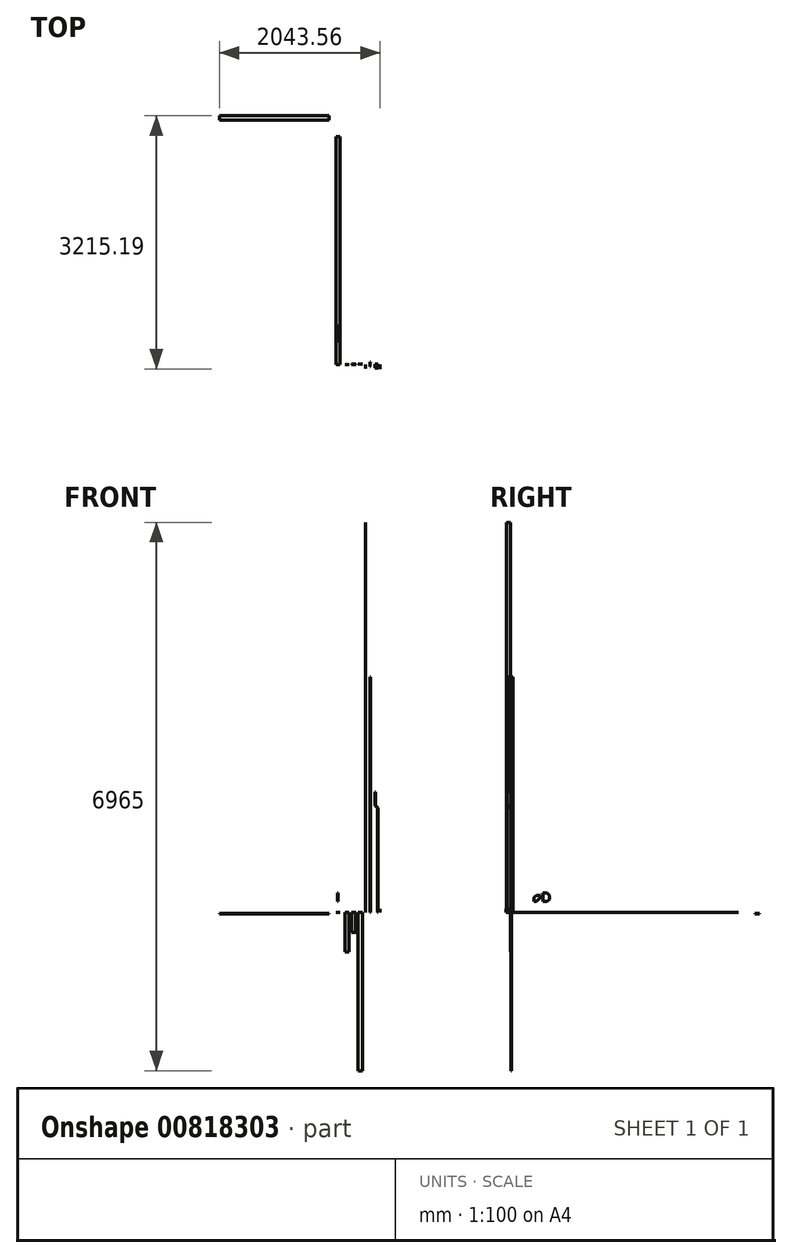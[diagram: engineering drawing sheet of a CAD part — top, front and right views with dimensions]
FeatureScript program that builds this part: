
annotation { "Feature Type Name" : "Feature", "Feature Type Description" : "" }
export const myFeature = defineFeature(function(context is Context, id is Id, definition is map)
    precondition{}
    {
        {
            var Q0;
            Q0=qCreatedBy(makeId("Front.planeOp"),FACE);
            var sketch = newSketch(context, id + "F0", { "sketchPlane" : qUnion([Q0])});
            skLineSegment(sketch, "E0.bottom", {"start": v(-26.5, 2.5) * mm, "end": v(26.5, 2.5) * mm});
            skLineSegment(sketch, "E0.left", {"start": v(-26.5, 2.5) * mm, "end": v(-26.5, -2.5) * mm});
            skLineSegment(sketch, "E0.right", {"start": v(26.5, 2.5) * mm, "end": v(26.5, -2.5) * mm});
            skPoint(sketch, "E0.middle", {"position": v(0, 0) * mm});
            skLineSegment(sketch, "E1", {"start": v(-26.5, -2.5) * mm, "end": v(-25, -2.5) * mm});
            skLineSegment(sketch, "E2", {"start": v(-25, -2.5) * mm, "end": v(-25, 1) * mm});
            skLineSegment(sketch, "E3", {"start": v(-25, 1) * mm, "end": v(25, 1) * mm});
            skLineSegment(sketch, "E4", {"start": v(25, 1) * mm, "end": v(25, -2.5) * mm});
            skLineSegment(sketch, "E5", {"start": v(25, -2.5) * mm, "end": v(26.5, -2.5) * mm});
            skSolve(sketch);
        }
        {
            var Q0;
            Q0 = qSketchRegion(id + "F0", true);
            extrude(context, id + "F1", {"entities" : qUnion([Q0]), "oppositeDirection" : true, "depth" : 2900 * mm, "offsetDistance" : 25 * mm});
        }
        {
            var Q0;
            Q0=makeQuery(id+"F1.opExtrude","SWEPT_FACE",FACE,{"disambiguationData":[OSD([sQuery(id+"F0.wireOp",EDGE,"E0.bottom")])]});
            var sketch = newSketch(context, id + "F2", { "sketchPlane" : qUnion([Q0])});
            skLineSegment(sketch, "E6", {"start": v(-51.63, 3107.68) * mm, "end": v(-15.26, 3067.27) * mm});
            skLineSegment(sketch, "E7", {"start": v(-51.63, 3107.68) * mm, "end": v(-51.63, 3157.68) * mm});
            skLineSegment(sketch, "E8", {"start": v(-51.63, 3157.68) * mm, "end": v(-21.63, 3157.68) * mm});
            skLineSegment(sketch, "E9", {"start": v(-15.26, 3067.27) * mm, "end": v(34.74, 3067.27) * mm});
            skLineSegment(sketch, "E10", {"start": v(34.74, 3067.27) * mm, "end": v(34.74, 3097.27) * mm});
            skLineSegment(sketch, "E11", {"start": v(34.74, 3097.27) * mm, "end": v(-21.63, 3157.68) * mm});
            skLineSegment(sketch, "E12.0", {"start": v(-53.13, 3107.1) * mm, "end": v(-15.93, 3065.77) * mm});
            skLineSegment(sketch, "E12.1", {"start": v(-53.13, 3159.18) * mm, "end": v(-20.97, 3159.18) * mm});
            skLineSegment(sketch, "E12.2", {"start": v(36.24, 3097.86) * mm, "end": v(-20.97, 3159.18) * mm});
            skLineSegment(sketch, "E12.3", {"start": v(-53.13, 3107.1) * mm, "end": v(-53.13, 3159.18) * mm});
            skLineSegment(sketch, "E12.4", {"start": v(36.24, 3065.77) * mm, "end": v(36.24, 3097.86) * mm});
            skLineSegment(sketch, "E12.5", {"start": v(-15.93, 3065.77) * mm, "end": v(36.24, 3065.77) * mm});
            skLineSegment(sketch, "E13", {"start": v(36.24, 3234.11) * mm, "end": v(-73.76, 3234.11) * mm});
            skLineSegment(sketch, "E14", {"start": v(36.24, 3234.11) * mm, "end": v(36.24, 3287.11) * mm});
            skLineSegment(sketch, "E15", {"start": v(-73.76, 3234.11) * mm, "end": v(-73.76, 3287.11) * mm});
            skLineSegment(sketch, "E16", {"start": v(-45.26, 3315.61) * mm, "end": v(7.74, 3315.61) * mm});
            skLineSegment(sketch, "E17", {"start": v(-18.76, 3234.11) * mm, "end": v(-18.76, 3315.61) * mm, "construction": true});
            skLineSegment(sketch, "E18", {"start": v(-18.76, 3315.61) * mm, "end": v(-18.76, 3324.5) * mm, "construction": true});
            skLineSegment(sketch, "E19", {"start": v(-73.76, 3287.11) * mm, "end": v(-45.26, 3315.61) * mm});
            skLineSegment(sketch, "E20", {"start": v(36.24, 3287.11) * mm, "end": v(7.74, 3315.61) * mm});
            skLineSegment(sketch, "E21.0", {"start": v(-72.26, 3286.5) * mm, "end": v(-44.2, 3314.55) * mm});
            skLineSegment(sketch, "E21.1", {"start": v(-72.26, 3234.11) * mm, "end": v(-72.26, 3286.5) * mm});
            skLineSegment(sketch, "E22.0", {"start": v(34.74, 3286.5) * mm, "end": v(6.68, 3314.55) * mm});
            skLineSegment(sketch, "E22.1", {"start": v(34.74, 3234.11) * mm, "end": v(34.74, 3286.5) * mm});
            skLineSegment(sketch, "E23", {"start": v(-45.26, 3315.61) * mm, "end": v(-44.2, 3314.55) * mm});
            skPoint(sketch, "E24.orphan", {"position": v(-43.14, 3315.61) * mm});
            skLineSegment(sketch, "E25", {"start": v(7.74, 3315.61) * mm, "end": v(6.68, 3314.55) * mm});
            skPoint(sketch, "E26.orphan", {"position": v(5.62, 3315.61) * mm});
            skLineSegment(sketch, "E27.0", {"start": v(36.24, 3235.61) * mm, "end": v(-73.76, 3235.61) * mm});
            skSolve(sketch);
        }
        {
            var Q0;
            Q0 = qSketchRegion(id + "F2", true);
            var Q1;
            Q1=makeQuery(id+"F2.imprint","IMPRINT",FACE,{"disambiguationData":[TD([[makeQuery(id+"F2.imprint","IMPRINT",EDGE,{"derivedFrom":sQuery(id+"F2.wireOp",EDGE,"E6")}),1.0]])]});
            extrude(context, id + "F3", {"entities" : qUnion([Q0, Q1]), "oppositeDirection" : true, "depth" : 1.5 * mm, "offsetDistance" : 25 * mm});
        }
        {
            var Q0;
            Q0=makeQuery(id+"F2.imprint","IMPRINT",FACE,{"disambiguationData":[TD([[makeQuery(id+"F2.imprint","IMPRINT",EDGE,{"derivedFrom":sQuery(id+"F2.wireOp",EDGE,"E6")}),1.0]])]});
            var sketch = newSketch(context, id + "F4", { "sketchPlane" : qUnion([Q0])});
            skLineSegment(sketch, "E28.0", {"start": v(-51.63, 3107.68) * mm, "end": v(-15.26, 3067.27) * mm});
            skLineSegment(sketch, "E29.0", {"start": v(-53.13, 3107.1) * mm, "end": v(-15.93, 3065.77) * mm});
            skLineSegment(sketch, "E30.0", {"start": v(-15.26, 3067.27) * mm, "end": v(36.24, 3067.27) * mm});
            skLineSegment(sketch, "E31.0", {"start": v(-15.93, 3065.77) * mm, "end": v(36.24, 3065.77) * mm});
            skPoint(sketch, "E32.0", {"position": v(-37.05, 3159.18) * mm});
            skLineSegment(sketch, "E33.0", {"start": v(-53.13, 3159.18) * mm, "end": v(-20.97, 3159.18) * mm});
            skLineSegment(sketch, "E34.0", {"start": v(-53.13, 3157.68) * mm, "end": v(-21.63, 3157.68) * mm});
            skLineSegment(sketch, "E35.0", {"start": v(36.24, 3097.86) * mm, "end": v(-20.97, 3159.18) * mm});
            skLineSegment(sketch, "E36.0", {"start": v(34.2, 3097.86) * mm, "end": v(-21.63, 3157.68) * mm});
            skLineSegment(sketch, "E37", {"start": v(-51.63, 3107.68) * mm, "end": v(-53.13, 3107.1) * mm});
            skLineSegment(sketch, "E38.0", {"start": v(-53.13, 3107.1) * mm, "end": v(-53.13, 3159.18) * mm, "construction": true});
            skLineSegment(sketch, "E39.0", {"start": v(36.24, 3065.77) * mm, "end": v(36.24, 3097.86) * mm, "construction": true});
            skPoint(sketch, "E40.orphan", {"position": v(-51.63, 3157.68) * mm});
            skLineSegment(sketch, "E41", {"start": v(-53.13, 3157.68) * mm, "end": v(-53.13, 3159.18) * mm});
            skPoint(sketch, "E42.orphan", {"position": v(34.74, 3067.27) * mm});
            skLineSegment(sketch, "E43", {"start": v(36.24, 3065.77) * mm, "end": v(36.24, 3067.27) * mm});
            skLineSegment(sketch, "E44", {"start": v(36.24, 3097.86) * mm, "end": v(34.2, 3097.86) * mm});
            skPoint(sketch, "E45.end.orphan", {"position": v(34.74, 3097.27) * mm});
            skPoint(sketch, "E46.0", {"position": v(-73.76, 3235.61) * mm});
            skPoint(sketch, "E47.0", {"position": v(-73.76, 3234.11) * mm});
            skPoint(sketch, "E48.0", {"position": v(36.24, 3235.61) * mm});
            skPoint(sketch, "E49.0", {"position": v(36.24, 3234.11) * mm});
            skLineSegment(sketch, "E50", {"start": v(36.24, 3235.61) * mm, "end": v(36.24, 3234.11) * mm});
            skLineSegment(sketch, "E51", {"start": v(-73.76, 3234.11) * mm, "end": v(-73.76, 3235.61) * mm});
            skLineSegment(sketch, "E52", {"start": v(36.24, 3235.61) * mm, "end": v(-73.76, 3235.61) * mm});
            skLineSegment(sketch, "E53", {"start": v(-73.76, 3234.11) * mm, "end": v(36.24, 3234.11) * mm});
            skPoint(sketch, "E54.0", {"position": v(36.24, 3287.11) * mm});
            skPoint(sketch, "E55.0", {"position": v(34.74, 3286.5) * mm});
            skPoint(sketch, "E56.0", {"position": v(-73.76, 3287.11) * mm});
            skPoint(sketch, "E57.0", {"position": v(-72.26, 3286.5) * mm});
            skLineSegment(sketch, "E58.0", {"start": v(-73.76, 3287.11) * mm, "end": v(-45.26, 3315.61) * mm});
            skLineSegment(sketch, "E59.0", {"start": v(-72.26, 3286.5) * mm, "end": v(-44.2, 3314.55) * mm});
            skLineSegment(sketch, "E60.0", {"start": v(-45.26, 3315.61) * mm, "end": v(-44.2, 3314.55) * mm});
            skPoint(sketch, "E61.0", {"position": v(7.74, 3315.61) * mm});
            skLineSegment(sketch, "E62.0", {"start": v(7.74, 3315.61) * mm, "end": v(6.68, 3314.55) * mm});
            skLineSegment(sketch, "E63.0", {"start": v(36.24, 3287.11) * mm, "end": v(7.74, 3315.61) * mm});
            skLineSegment(sketch, "E64.0", {"start": v(34.74, 3286.5) * mm, "end": v(6.68, 3314.55) * mm});
            skLineSegment(sketch, "E65", {"start": v(34.74, 3286.5) * mm, "end": v(36.24, 3287.11) * mm});
            skLineSegment(sketch, "E66", {"start": v(-73.76, 3287.11) * mm, "end": v(-72.26, 3286.5) * mm});
            skSolve(sketch);
        }
        {
            var Q0;
            Q0 = qSketchRegion(id + "F4", true);
            extrude(context, id + "F5", {"entities" : qUnion([Q0]), "operationType" : NewBodyOperationType.ADD, "oppositeDirection" : true, "depth" : 5 * mm, "offsetDistance" : 25 * mm});
        }
        {
            var Q0;
            Q0=makeQuery(id+"F1.opExtrude","SWEPT_FACE",FACE,{"disambiguationData":[OSD([sQuery(id+"F0.wireOp",EDGE,"E0.right")])]});
            cPlane(context, id + "F6", {"entities" : qUnion([Q0]), "cplaneType" : CPlaneType.OFFSET, "offset" : 143 * mm, "oppositeDirection" : true, "width" : 150 * mm, "height" : 150 * mm});
        }
        {
            var Q0;
            Q0=qCreatedBy(id+"F6.planeOp",FACE);
            var sketch = newSketch(context, id + "F7", { "sketchPlane" : qUnion([Q0])});
            skLineSegment(sketch, "E67", {"start": v(3109.74, -14.83) * mm, "end": v(3162.74, -14.83) * mm});
            skLineSegment(sketch, "E68", {"start": v(3109.74, -14.83) * mm, "end": v(3109.74, -19.83) * mm});
            skLineSegment(sketch, "E69", {"start": v(3109.74, -19.83) * mm, "end": v(3111.24, -19.83) * mm});
            skLineSegment(sketch, "E70", {"start": v(3111.24, -19.83) * mm, "end": v(3111.24, -16.33) * mm});
            skLineSegment(sketch, "E71", {"start": v(3111.24, -16.33) * mm, "end": v(3161.24, -16.33) * mm});
            skLineSegment(sketch, "E72", {"start": v(3161.24, -16.33) * mm, "end": v(3161.24, -19.83) * mm});
            skLineSegment(sketch, "E73", {"start": v(3161.24, -19.83) * mm, "end": v(3162.74, -19.83) * mm});
            skLineSegment(sketch, "E74", {"start": v(3162.74, -19.83) * mm, "end": v(3162.74, -14.83) * mm});
            skSolve(sketch);
        }
        {
            var Q0;
            Q0 = qSketchRegion(id + "F7", true);
            extrude(context, id + "F8", {"entities" : qUnion([Q0]), "oppositeDirection" : true, "depth" : 1390 * mm, "offsetDistance" : 25 * mm});
        }
        {
            var Q0;
            Q0=makeQuery(id+"F3.opExtrude","SWEPT_BODY",BODY,{"disambiguationData":[OSD([sQuery(id+"F2.wireOp",EDGE,"E12.0"),sQuery(id+"F2.wireOp",EDGE,"E12.1"),sQuery(id+"F2.wireOp",EDGE,"E12.2"),sQuery(id+"F2.wireOp",EDGE,"E12.3"),sQuery(id+"F2.wireOp",EDGE,"E12.4"),sQuery(id+"F2.wireOp",EDGE,"E12.5")])]});
            deleteBodies(context, id + "F9", {"entities" : qUnion([Q0])});
        }
        {
            var Q0;
            Q0=makeQuery(id+"F3.opExtrude","SWEPT_BODY",BODY,{"disambiguationData":[OSD([sQuery(id+"F2.wireOp",EDGE,"E13"),sQuery(id+"F2.wireOp",EDGE,"E14"),sQuery(id+"F2.wireOp",EDGE,"E15"),sQuery(id+"F2.wireOp",EDGE,"E16"),sQuery(id+"F2.wireOp",EDGE,"E19"),sQuery(id+"F2.wireOp",EDGE,"E20")])]});
            deleteBodies(context, id + "F10", {"entities" : qUnion([Q0])});
        }
        {
            var Q0;
            Q0=qCreatedBy(makeId("Top.planeOp"),FACE);
            var sketch = newSketch(context, id + "F11", { "sketchPlane" : qUnion([Q0])});
            skLineSegment(sketch, "E75", {"start": v(88.68, 0) * mm, "end": v(88.68, 5) * mm});
            skLineSegment(sketch, "E76", {"start": v(88.68, 5) * mm, "end": v(141.68, 5) * mm});
            skLineSegment(sketch, "E77", {"start": v(141.68, 5) * mm, "end": v(141.68, 0) * mm});
            skLineSegment(sketch, "E78", {"start": v(141.68, 0) * mm, "end": v(140.18, 0) * mm});
            skLineSegment(sketch, "E79", {"start": v(140.18, 0) * mm, "end": v(140.18, 3.5) * mm});
            skLineSegment(sketch, "E80", {"start": v(140.18, 3.5) * mm, "end": v(90.18, 3.5) * mm});
            skLineSegment(sketch, "E81", {"start": v(90.18, 3.5) * mm, "end": v(90.18, 0) * mm});
            skLineSegment(sketch, "E82", {"start": v(90.18, 0) * mm, "end": v(88.68, 0) * mm});
            skSolve(sketch);
        }
        {
            var Q0;
            Q0 = qSketchRegion(id + "F11", true);
            extrude(context, id + "F12", {"entities" : qUnion([Q0]), "oppositeDirection" : true, "depth" : 500 * mm, "offsetDistance" : 25 * mm});
        }
        {
            var Q0;
            Q0=qCreatedBy(makeId("Top.planeOp"),FACE);
            var sketch = newSketch(context, id + "F13", { "sketchPlane" : qUnion([Q0])});
            skLineSegment(sketch, "E83", {"start": v(173.66, 1.16) * mm, "end": v(173.66, 6.16) * mm});
            skLineSegment(sketch, "E84", {"start": v(173.66, 6.16) * mm, "end": v(226.66, 6.16) * mm});
            skLineSegment(sketch, "E85", {"start": v(226.66, 6.16) * mm, "end": v(226.66, 1.16) * mm});
            skLineSegment(sketch, "E86", {"start": v(226.66, 1.16) * mm, "end": v(225.16, 1.16) * mm});
            skLineSegment(sketch, "E87", {"start": v(225.16, 1.16) * mm, "end": v(225.16, 4.66) * mm});
            skLineSegment(sketch, "E88", {"start": v(225.16, 4.66) * mm, "end": v(175.16, 4.66) * mm});
            skLineSegment(sketch, "E89", {"start": v(175.16, 4.66) * mm, "end": v(175.16, 1.16) * mm});
            skLineSegment(sketch, "E90", {"start": v(175.16, 1.16) * mm, "end": v(173.66, 1.16) * mm});
            skSolve(sketch);
        }
        {
            var Q0;
            Q0 = qSketchRegion(id + "F13", true);
            extrude(context, id + "F14", {"entities" : qUnion([Q0]), "oppositeDirection" : true, "depth" : 255 * mm, "offsetDistance" : 25 * mm});
        }
        {
            var Q0;
            Q0=qCreatedBy(makeId("Top.planeOp"),FACE);
            var sketch = newSketch(context, id + "F15", { "sketchPlane" : qUnion([Q0])});
            skLineSegment(sketch, "E91", {"start": v(308.98, 12) * mm, "end": v(308.98, 7) * mm});
            skLineSegment(sketch, "E92", {"start": v(308.98, 7) * mm, "end": v(255.98, 7) * mm});
            skLineSegment(sketch, "E93", {"start": v(255.98, 7) * mm, "end": v(255.98, 12) * mm});
            skLineSegment(sketch, "E94", {"start": v(255.98, 12) * mm, "end": v(257.48, 12) * mm});
            skLineSegment(sketch, "E95", {"start": v(257.48, 12) * mm, "end": v(257.48, 8.5) * mm});
            skLineSegment(sketch, "E96", {"start": v(257.48, 8.5) * mm, "end": v(307.48, 8.5) * mm});
            skLineSegment(sketch, "E97", {"start": v(307.48, 8.5) * mm, "end": v(307.48, 12) * mm});
            skLineSegment(sketch, "E98", {"start": v(307.48, 12) * mm, "end": v(308.98, 12) * mm});
            skSolve(sketch);
        }
        {
            var Q0;
            Q0 = qSketchRegion(id + "F15", true);
            extrude(context, id + "F16", {"entities" : qUnion([Q0]), "oppositeDirection" : true, "depth" : 2010 * mm, "offsetDistance" : 25 * mm});
        }
        {
            var Q0;
            Q0=qCreatedBy(makeId("Top.planeOp"),FACE);
            var sketch = newSketch(context, id + "F17", { "sketchPlane" : qUnion([Q0])});
            skLineSegment(sketch, "E99", {"start": v(351.99, -49.21) * mm, "end": v(346.99, -49.21) * mm});
            skLineSegment(sketch, "E100", {"start": v(346.99, -49.21) * mm, "end": v(346.99, 3.79) * mm});
            skLineSegment(sketch, "E101", {"start": v(346.99, 3.79) * mm, "end": v(351.99, 3.79) * mm});
            skLineSegment(sketch, "E102", {"start": v(351.99, 3.79) * mm, "end": v(351.99, 2.29) * mm});
            skLineSegment(sketch, "E103", {"start": v(351.99, 2.29) * mm, "end": v(348.49, 2.29) * mm});
            skLineSegment(sketch, "E104", {"start": v(348.49, 2.29) * mm, "end": v(348.49, -47.71) * mm});
            skLineSegment(sketch, "E105", {"start": v(348.49, -47.71) * mm, "end": v(351.99, -47.71) * mm});
            skLineSegment(sketch, "E106", {"start": v(351.99, -47.71) * mm, "end": v(351.99, -49.21) * mm});
            skSolve(sketch);
        }
        {
            var Q0;
            Q0 = qSketchRegion(id + "F17", true);
            extrude(context, id + "F18", {"entities" : qUnion([Q0]), "depth" : 4955 * mm, "offsetDistance" : 25 * mm});
        }
        {
            var Q0;
            Q0=qCreatedBy(makeId("Top.planeOp"),FACE);
            var sketch = newSketch(context, id + "F19", { "sketchPlane" : qUnion([Q0])});
            skLineSegment(sketch, "E107", {"start": v(411.7, -21.33) * mm, "end": v(406.7, -21.33) * mm});
            skLineSegment(sketch, "E108", {"start": v(406.7, -21.33) * mm, "end": v(406.7, 31.67) * mm});
            skLineSegment(sketch, "E109", {"start": v(406.7, 31.67) * mm, "end": v(411.7, 31.67) * mm});
            skLineSegment(sketch, "E110", {"start": v(411.7, 31.67) * mm, "end": v(411.7, 30.17) * mm});
            skLineSegment(sketch, "E111", {"start": v(411.7, 30.17) * mm, "end": v(408.2, 30.17) * mm});
            skLineSegment(sketch, "E112", {"start": v(408.2, 30.17) * mm, "end": v(408.2, -19.83) * mm});
            skLineSegment(sketch, "E113", {"start": v(408.2, -19.83) * mm, "end": v(411.7, -19.83) * mm});
            skLineSegment(sketch, "E114", {"start": v(411.7, -19.83) * mm, "end": v(411.7, -21.33) * mm});
            skSolve(sketch);
        }
        {
            var Q0;
            Q0 = qSketchRegion(id + "F19", true);
            extrude(context, id + "F20", {"entities" : qUnion([Q0]), "depth" : 2990 * mm, "offsetDistance" : 25 * mm});
        }
        {
            var Q0;
            Q0=qCreatedBy(makeId("Top.planeOp"),FACE);
            var sketch = newSketch(context, id + "F21", { "sketchPlane" : qUnion([Q0])});
            skLineSegment(sketch, "E115", {"start": v(509.52, -43.75) * mm, "end": v(504.52, -43.75) * mm});
            skLineSegment(sketch, "E116", {"start": v(504.52, -43.75) * mm, "end": v(504.52, 9.25) * mm});
            skLineSegment(sketch, "E117", {"start": v(504.52, 9.25) * mm, "end": v(509.52, 9.25) * mm});
            skLineSegment(sketch, "E118", {"start": v(509.52, 9.25) * mm, "end": v(509.52, 7.75) * mm});
            skLineSegment(sketch, "E119", {"start": v(509.52, 7.75) * mm, "end": v(506.02, 7.75) * mm});
            skLineSegment(sketch, "E120", {"start": v(506.02, 7.75) * mm, "end": v(506.02, -42.25) * mm});
            skLineSegment(sketch, "E121", {"start": v(506.02, -42.25) * mm, "end": v(509.52, -42.25) * mm});
            skLineSegment(sketch, "E122", {"start": v(509.52, -42.25) * mm, "end": v(509.52, -43.75) * mm});
            skSolve(sketch);
        }
        {
            var Q0;
            Q0 = qSketchRegion(id + "F21", true);
            extrude(context, id + "F22", {"entities" : qUnion([Q0]), "depth" : 1325 * mm, "offsetDistance" : 25 * mm});
        }
        {
            var Q0;
            Q0=makeQuery(id+"F22.opExtrude","SWEPT_FACE",FACE,{"disambiguationData":[OSD([sQuery(id+"F21.wireOp",EDGE,"E117")])]});
            var sketch = newSketch(context, id + "F23", { "sketchPlane" : qUnion([Q0])});
            skPoint(sketch, "E123.0", {"position": v(-504.52, 1325) * mm});
            skLineSegment(sketch, "E124", {"start": v(-504.52, 1325) * mm, "end": v(-469.52, 1360) * mm});
            skLineSegment(sketch, "E125", {"start": v(-469.52, 1360) * mm, "end": v(-469.52, 1530) * mm});
            skLineSegment(sketch, "E126.0", {"start": v(-506.64, 1325) * mm, "end": v(-471.02, 1360.62) * mm});
            skLineSegment(sketch, "E127.0", {"start": v(-471.02, 1360.62) * mm, "end": v(-471.02, 1530) * mm});
            skLineSegment(sketch, "E128", {"start": v(-469.52, 1530) * mm, "end": v(-471.02, 1530) * mm});
            skLineSegment(sketch, "E129", {"start": v(-504.52, 1325) * mm, "end": v(-506.64, 1325) * mm});
            skSolve(sketch);
        }
        {
            var Q0;
            Q0 = qSketchRegion(id + "F23", true);
            extrude(context, id + "F24", {"entities" : qUnion([Q0]), "operationType" : NewBodyOperationType.ADD, "oppositeDirection" : true, "depth" : 53 * mm, "offsetDistance" : 25 * mm});
        }
        {
            var Q0;
            Q0=makeQuery(id+"F24.boolean.opBoolean","MERGE",FACE,{"derivedFrom":[makeQuery(id+"F22.opExtrude","SWEPT_FACE",FACE,{"disambiguationData":[OSD([sQuery(id+"F21.wireOp",EDGE,"E117")])]}),makeQuery(id+"F24.opExtrude","CAP_FACE",FACE,{"disambiguationData":[OSD([sQuery(id+"F23.wireOp",EDGE,"E124"),sQuery(id+"F23.wireOp",EDGE,"E125"),sQuery(id+"F23.wireOp",EDGE,"E126.0"),sQuery(id+"F23.wireOp",EDGE,"E127.0"),sQuery(id+"F23.wireOp",EDGE,"E128"),sQuery(id+"F23.wireOp",EDGE,"E129")])],"isStart":true})]});
            var sketch = newSketch(context, id + "F25", { "sketchPlane" : qUnion([Q0])});
            skLineSegment(sketch, "E130", {"start": v(-469.52, 1530) * mm, "end": v(-474.52, 1530) * mm});
            skLineSegment(sketch, "E131", {"start": v(-474.52, 1530) * mm, "end": v(-474.52, 1362.07) * mm});
            skLineSegment(sketch, "E132.0", {"start": v(-509.52, 1327.07) * mm, "end": v(-474.52, 1362.07) * mm});
            skPoint(sketch, "E133.0", {"position": v(-504.52, 1325) * mm});
            skPoint(sketch, "E134.0", {"position": v(-509.52, 1325) * mm});
            skLineSegment(sketch, "E135", {"start": v(-509.52, 1325) * mm, "end": v(-509.52, 1327.07) * mm});
            skLineSegment(sketch, "E136", {"start": v(-504.52, 1325) * mm, "end": v(-509.52, 1325) * mm});
            skLineSegment(sketch, "E137.0", {"start": v(-469.52, 1360) * mm, "end": v(-469.52, 1530) * mm});
            skLineSegment(sketch, "E138.0", {"start": v(-504.52, 1325) * mm, "end": v(-469.52, 1360) * mm});
            skSolve(sketch);
        }
        {
            var Q0;
            Q0 = qSketchRegion(id + "F25", true);
            extrude(context, id + "F26", {"entities" : qUnion([Q0]), "operationType" : NewBodyOperationType.ADD, "oppositeDirection" : true, "depth" : 1.5 * mm, "offsetDistance" : 25 * mm});
        }
        {
            var Q0;
            Q0=makeQuery(id+"F24.boolean.opBoolean","MERGE",FACE,{"derivedFrom":[makeQuery(id+"F22.opExtrude","SWEPT_FACE",FACE,{"disambiguationData":[OSD([sQuery(id+"F21.wireOp",EDGE,"E115")])]}),makeQuery(id+"F24.opExtrude","CAP_FACE",FACE,{"disambiguationData":[OSD([sQuery(id+"F23.wireOp",EDGE,"E124"),sQuery(id+"F23.wireOp",EDGE,"E125"),sQuery(id+"F23.wireOp",EDGE,"E126.0"),sQuery(id+"F23.wireOp",EDGE,"E127.0"),sQuery(id+"F23.wireOp",EDGE,"E128"),sQuery(id+"F23.wireOp",EDGE,"E129")])],"isStart":false})]});
            var sketch = newSketch(context, id + "F27", { "sketchPlane" : qUnion([Q0])});
            skLineSegment(sketch, "E139.0", {"start": v(509.52, 1327.07) * mm, "end": v(474.52, 1362.07) * mm});
            skPoint(sketch, "E140.0", {"position": v(487.02, 1342.5) * mm});
            skLineSegment(sketch, "E141.0", {"start": v(504.52, 1325) * mm, "end": v(469.52, 1360) * mm});
            skLineSegment(sketch, "E142.0", {"start": v(469.52, 1360) * mm, "end": v(469.52, 1530) * mm});
            skLineSegment(sketch, "E143.0", {"start": v(474.52, 1530) * mm, "end": v(474.52, 1362.07) * mm});
            skLineSegment(sketch, "E144.0", {"start": v(469.52, 1530) * mm, "end": v(471.02, 1530) * mm});
            skLineSegment(sketch, "E145.0", {"start": v(471.02, 1530) * mm, "end": v(474.52, 1530) * mm});
            skLineSegment(sketch, "E146.0", {"start": v(509.52, 1325) * mm, "end": v(506.64, 1325) * mm});
            skLineSegment(sketch, "E147", {"start": v(509.52, 1325) * mm, "end": v(509.52, 1327.07) * mm});
            skLineSegment(sketch, "E148", {"start": v(506.64, 1325) * mm, "end": v(504.52, 1325) * mm});
            skSolve(sketch);
        }
        {
            var Q0;
            Q0 = qSketchRegion(id + "F27", true);
            extrude(context, id + "F28", {"entities" : qUnion([Q0]), "operationType" : NewBodyOperationType.ADD, "oppositeDirection" : true, "depth" : 1.5 * mm, "offsetDistance" : 25 * mm});
        }
        {
            var Q0;
            Q0=qCreatedBy(makeId("Right.planeOp"),FACE);
            var sketch = newSketch(context, id + "F29", { "sketchPlane" : qUnion([Q0])});
            skLineSegment(sketch, "E149", {"start": v(300.98, 139.15) * mm, "end": v(300.98, 189.15) * mm});
            skLineSegment(sketch, "E150", {"start": v(300.98, 139.15) * mm, "end": v(330.98, 139.15) * mm});
            skLineSegment(sketch, "E151", {"start": v(300.98, 189.15) * mm, "end": v(330.98, 219.15) * mm});
            skLineSegment(sketch, "E152", {"start": v(330.98, 219.15) * mm, "end": v(380.98, 219.15) * mm});
            skLineSegment(sketch, "E153", {"start": v(380.98, 219.15) * mm, "end": v(380.98, 189.15) * mm});
            skLineSegment(sketch, "E154", {"start": v(380.98, 189.15) * mm, "end": v(330.98, 139.15) * mm});
            skLineSegment(sketch, "E155.0", {"start": v(300.98, 137.65) * mm, "end": v(331.6, 137.65) * mm});
            skLineSegment(sketch, "E155.1", {"start": v(382.48, 188.53) * mm, "end": v(331.6, 137.65) * mm});
            skLineSegment(sketch, "E155.2", {"start": v(382.48, 219.15) * mm, "end": v(382.48, 188.53) * mm});
            skLineSegment(sketch, "E156", {"start": v(380.98, 219.15) * mm, "end": v(382.48, 219.15) * mm});
            skLineSegment(sketch, "E157", {"start": v(300.98, 137.65) * mm, "end": v(300.98, 139.15) * mm});
            skLineSegment(sketch, "E158.1", {"start": v(300.98, 190.65) * mm, "end": v(329.48, 219.15) * mm});
            skLineSegment(sketch, "E159", {"start": v(330.98, 219.15) * mm, "end": v(329.48, 219.15) * mm});
            skLineSegment(sketch, "E160", {"start": v(300.98, 189.15) * mm, "end": v(300.98, 190.65) * mm});
            skSolve(sketch);
        }
        {
            var Q0;
            Q0 = qSketchRegion(id + "F29", true);
            extrude(context, id + "F30", {"entities" : qUnion([Q0]), "oppositeDirection" : true, "depth" : 1.5 * mm, "offsetDistance" : 25 * mm});
        }
        {
            var Q0;
            Q0=makeQuery(id+"F29.imprint","IMPRINT",FACE,{"disambiguationData":[TD([[makeQuery(id+"F29.imprint","IMPRINT",EDGE,{"derivedFrom":sQuery(id+"F29.wireOp",EDGE,"E149")}),-1.0]])]});
            var sketch = newSketch(context, id + "F31", { "sketchPlane" : qUnion([Q0])});
            skLineSegment(sketch, "E161.0", {"start": v(300.98, 189.15) * mm, "end": v(330.98, 219.15) * mm});
            skLineSegment(sketch, "E162.0", {"start": v(300.98, 190.65) * mm, "end": v(329.48, 219.15) * mm});
            skLineSegment(sketch, "E163.0", {"start": v(382.48, 219.15) * mm, "end": v(382.48, 188.53) * mm});
            skLineSegment(sketch, "E164.0", {"start": v(380.98, 219.15) * mm, "end": v(380.98, 189.15) * mm});
            skLineSegment(sketch, "E165.0", {"start": v(382.48, 188.53) * mm, "end": v(331.6, 137.65) * mm});
            skLineSegment(sketch, "E166.0", {"start": v(380.98, 189.15) * mm, "end": v(330.98, 139.15) * mm});
            skLineSegment(sketch, "E167.0", {"start": v(300.98, 137.65) * mm, "end": v(331.6, 137.65) * mm});
            skLineSegment(sketch, "E168.0", {"start": v(300.98, 139.15) * mm, "end": v(330.98, 139.15) * mm});
            skLineSegment(sketch, "E169", {"start": v(300.98, 139.15) * mm, "end": v(300.98, 137.65) * mm});
            skLineSegment(sketch, "E170", {"start": v(380.98, 219.15) * mm, "end": v(382.48, 219.15) * mm});
            skLineSegment(sketch, "E171", {"start": v(329.48, 219.15) * mm, "end": v(330.98, 219.15) * mm});
            skLineSegment(sketch, "E172", {"start": v(300.98, 189.15) * mm, "end": v(300.98, 190.65) * mm});
            skSolve(sketch);
        }
        {
            var Q0;
            Q0 = qSketchRegion(id + "F31", true);
            extrude(context, id + "F32", {"entities" : qUnion([Q0]), "operationType" : NewBodyOperationType.ADD, "oppositeDirection" : true, "depth" : 5 * mm, "offsetDistance" : 25 * mm});
        }
        {
            var Q0;
            Q0=makeQuery(id+"F30.opExtrude","CAP_FACE",FACE,{"disambiguationData":[OSD([sQuery(id+"F29.wireOp",EDGE,"E149"),sQuery(id+"F29.wireOp",EDGE,"E152"),sQuery(id+"F29.wireOp",EDGE,"E155.0"),sQuery(id+"F29.wireOp",EDGE,"E155.1"),sQuery(id+"F29.wireOp",EDGE,"E155.2"),sQuery(id+"F29.wireOp",EDGE,"E156"),sQuery(id+"F29.wireOp",EDGE,"E157"),sQuery(id+"F29.wireOp",EDGE,"E158.1"),sQuery(id+"F29.wireOp",EDGE,"E159"),sQuery(id+"F29.wireOp",EDGE,"E160")])],"isStart":true});
            var sketch = newSketch(context, id + "F33", { "sketchPlane" : qUnion([Q0])});
            skLineSegment(sketch, "E173", {"start": v(414.53, 137.65) * mm, "end": v(414.53, 247.65) * mm});
            skLineSegment(sketch, "E174", {"start": v(414.53, 137.65) * mm, "end": v(464.53, 137.65) * mm});
            skLineSegment(sketch, "E175", {"start": v(464.53, 137.65) * mm, "end": v(494.53, 167.65) * mm});
            skLineSegment(sketch, "E176", {"start": v(494.53, 167.65) * mm, "end": v(494.53, 217.65) * mm});
            skLineSegment(sketch, "E177", {"start": v(494.53, 217.65) * mm, "end": v(464.53, 247.65) * mm});
            skLineSegment(sketch, "E178", {"start": v(464.53, 247.65) * mm, "end": v(414.53, 247.65) * mm});
            skLineSegment(sketch, "E179.0", {"start": v(413.03, 137.65) * mm, "end": v(413.03, 247.65) * mm});
            skLineSegment(sketch, "E180", {"start": v(464.53, 137.65) * mm, "end": v(466.03, 137.65) * mm});
            skLineSegment(sketch, "E181", {"start": v(494.53, 167.65) * mm, "end": v(494.53, 166.15) * mm});
            skLineSegment(sketch, "E182", {"start": v(494.53, 217.65) * mm, "end": v(494.53, 219.15) * mm});
            skLineSegment(sketch, "E183", {"start": v(464.53, 247.65) * mm, "end": v(466.03, 247.65) * mm});
            skLineSegment(sketch, "E184", {"start": v(494.53, 166.15) * mm, "end": v(466.03, 137.65) * mm});
            skLineSegment(sketch, "E185", {"start": v(466.03, 247.65) * mm, "end": v(494.53, 219.15) * mm});
            skLineSegment(sketch, "E186", {"start": v(413.03, 247.65) * mm, "end": v(414.53, 247.65) * mm});
            skLineSegment(sketch, "E187", {"start": v(413.03, 137.65) * mm, "end": v(414.53, 137.65) * mm});
            skLineSegment(sketch, "E188", {"start": v(466.03, 137.65) * mm, "end": v(464.53, 137.65) * mm});
            skSolve(sketch);
        }
        {
            var Q0;
            Q0 = qSketchRegion(id + "F33", true);
            extrude(context, id + "F34", {"entities" : qUnion([Q0]), "oppositeDirection" : true, "depth" : 1.5 * mm, "offsetDistance" : 25 * mm});
        }
        {
            var Q0;
            Q0=makeQuery(id+"F33.imprint","IMPRINT",FACE,{"disambiguationData":[TD([[makeQuery(id+"F33.imprint","IMPRINT",EDGE,{"derivedFrom":sQuery(id+"F33.wireOp",EDGE,"E173")}),-1.0]])]});
            var sketch = newSketch(context, id + "F35", { "sketchPlane" : qUnion([Q0])});
            skLineSegment(sketch, "E189.0", {"start": v(414.53, 137.65) * mm, "end": v(414.53, 247.65) * mm});
            skLineSegment(sketch, "E190.0", {"start": v(413.03, 137.65) * mm, "end": v(413.03, 247.65) * mm});
            skLineSegment(sketch, "E191.0", {"start": v(494.53, 217.65) * mm, "end": v(464.53, 247.65) * mm});
            skLineSegment(sketch, "E192.0", {"start": v(466.03, 247.65) * mm, "end": v(494.53, 219.15) * mm});
            skLineSegment(sketch, "E193.0", {"start": v(494.53, 166.15) * mm, "end": v(466.03, 137.65) * mm});
            skLineSegment(sketch, "E194.0", {"start": v(464.53, 137.65) * mm, "end": v(494.53, 167.65) * mm});
            skLineSegment(sketch, "E195", {"start": v(413.03, 247.65) * mm, "end": v(414.53, 247.65) * mm});
            skLineSegment(sketch, "E196", {"start": v(466.03, 247.65) * mm, "end": v(464.53, 247.65) * mm});
            skLineSegment(sketch, "E197", {"start": v(494.53, 219.15) * mm, "end": v(494.53, 217.65) * mm});
            skLineSegment(sketch, "E198", {"start": v(413.03, 137.65) * mm, "end": v(414.53, 137.65) * mm});
            skLineSegment(sketch, "E199", {"start": v(464.53, 137.65) * mm, "end": v(466.03, 137.65) * mm});
            skLineSegment(sketch, "E200", {"start": v(494.53, 167.65) * mm, "end": v(494.53, 166.15) * mm});
            skSolve(sketch);
        }
        {
            var Q0;
            Q0 = qSketchRegion(id + "F35", true);
            extrude(context, id + "F36", {"entities" : qUnion([Q0]), "operationType" : NewBodyOperationType.ADD, "oppositeDirection" : true, "depth" : 5 * mm, "offsetDistance" : 25 * mm});
        }
        {
            var Q0;
            Q0=qCreatedBy(makeId("Top.planeOp"),FACE);
            var sketch = newSketch(context, id + "F37", { "sketchPlane" : qUnion([Q0])});
            skLineSegment(sketch, "E201", {"start": v(537.06, -52.45) * mm, "end": v(532.06, -52.45) * mm});
            skLineSegment(sketch, "E202", {"start": v(532.06, -52.45) * mm, "end": v(532.06, 0.55) * mm});
            skLineSegment(sketch, "E203", {"start": v(532.06, 0.55) * mm, "end": v(537.06, 0.55) * mm});
            skLineSegment(sketch, "E204", {"start": v(537.06, 0.55) * mm, "end": v(537.06, -0.95) * mm});
            skLineSegment(sketch, "E205", {"start": v(537.06, -0.95) * mm, "end": v(533.56, -0.95) * mm});
            skLineSegment(sketch, "E206", {"start": v(533.56, -0.95) * mm, "end": v(533.56, -50.95) * mm});
            skLineSegment(sketch, "E207", {"start": v(533.56, -50.95) * mm, "end": v(537.06, -50.95) * mm});
            skLineSegment(sketch, "E208", {"start": v(537.06, -50.95) * mm, "end": v(537.06, -52.45) * mm});
            skSolve(sketch);
        }
        {
            var Q0;
            Q0 = qSketchRegion(id + "F37", true);
            extrude(context, id + "F38", {"entities" : qUnion([Q0]), "depth" : 42.43 * mm, "offsetDistance" : 25 * mm});
        }
    });
